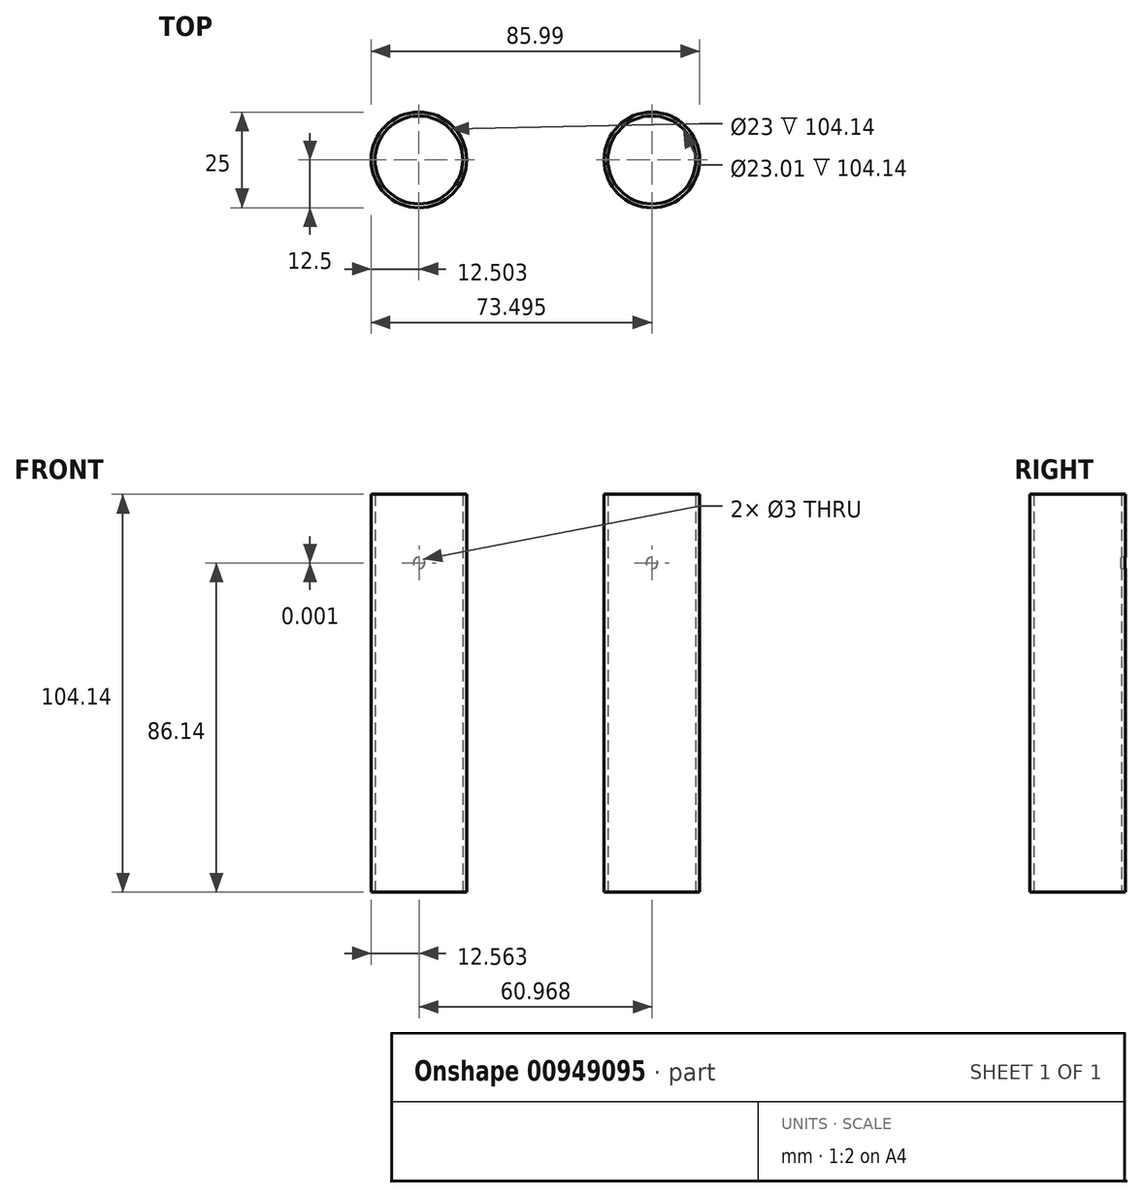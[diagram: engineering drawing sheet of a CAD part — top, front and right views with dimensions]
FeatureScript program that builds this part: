
annotation { "Feature Type Name" : "Feature", "Feature Type Description" : "" }
export const myFeature = defineFeature(function(context is Context, id is Id, definition is map)
    precondition{}
    {
        {
            var Q0;
            Q0=qCreatedBy(makeId("Top.planeOp"),FACE);
            var sketch = newSketch(context, id + "F0", { "sketchPlane" : qUnion([Q0])});
            skCircle(sketch, "E0", {"center": v(-36.28, 0) * mm, "radius": 11.5 * mm});
            skCircle(sketch, "E1", {"center": v(24.71, 0) * mm, "radius": 11.5 * mm});
            skPoint(sketch, "E2", {"position": v(13.2, 0) * mm});
            skPoint(sketch, "E3", {"position": v(-24.78, 0) * mm});
            skCircle(sketch, "E4", {"center": v(-36.28, 0) * mm, "radius": 12.5 * mm});
            skCircle(sketch, "E5", {"center": v(24.71, 0) * mm, "radius": 12.5 * mm});
            skPoint(sketch, "E6", {"position": v(-23.78, 0) * mm});
            skPoint(sketch, "E7", {"position": v(12.21, 0) * mm});
            skSolve(sketch);
        }
        {
            var Q0;
            Q0=makeQuery(id+"F0.imprint","IMPRINT",FACE,{"disambiguationData":[TD([[makeQuery(id+"F0.imprint","IMPRINT",EDGE,{"derivedFrom":sQuery(id+"F0.wireOp",EDGE,"E1")}),-1.0]])]});
            var Q1;
            Q1=makeQuery(id+"F0.imprint","IMPRINT",FACE,{"disambiguationData":[TD([[makeQuery(id+"F0.imprint","IMPRINT",EDGE,{"derivedFrom":sQuery(id+"F0.wireOp",EDGE,"E0")}),-1.0]])]});
            extrude(context, id + "F1", {"entities" : qUnion([Q0, Q1]), "depth" : 104.14 * mm, "offsetDistance" : 25.4 * mm, "symmetric" : true});
        }
        {
            var Q0;
            Q0=qCreatedBy(makeId("Front.planeOp"),FACE);
            var sketch = newSketch(context, id + "F2", { "sketchPlane" : qUnion([Q0])});
            skCircle(sketch, "E8", {"center": v(24.75, 34.07) * mm, "radius": 1.5 * mm});
            skCircle(sketch, "E9", {"center": v(-36.22, 34.07) * mm, "radius": 1.5 * mm});
            skLineSegment(sketch, "E10", {"start": v(37.21, 0) * mm, "end": v(12.3, 0) * mm});
            skPoint(sketch, "E11", {"position": v(24.75, 0) * mm});
            skLineSegment(sketch, "E12", {"start": v(-23.65, 0) * mm, "end": v(-48.79, 0) * mm});
            skPoint(sketch, "E13", {"position": v(-36.22, 0) * mm});
            skLineSegment(sketch, "E14", {"start": v(-36.22, 0) * mm, "end": v(-36.22, 34.07) * mm});
            skLineSegment(sketch, "E15", {"start": v(24.75, 0) * mm, "end": v(24.75, 34.07) * mm});
            skSolve(sketch);
        }
        {
            var Q0;
            {var subQ0=sQuery(id+"F2.wireOp",EDGE,"UVFeuSc1-rwqc-uxTH-lkc2-MKaSKzfGkuLp");var subQ1=sQuery(id+"F2.wireOp",EDGE,"E8");var subQ2=makeQuery(id+"F2.imprint","INTERSECT",VERTEX,{"disambiguationData":[OD(1.0)],"derivedFrom":[subQ1,subQ0]});Q0=makeQuery(id+"F2.imprint","IMPRINT",FACE,{"disambiguationData":[TD([[makeQuery(id+"F2.imprint","IMPRINT",EDGE,{"disambiguationData":[TD([[subQ2,1.0]])],"derivedFrom":subQ1}),1.0]])]});}
            var Q1;
            {var subQ0=sQuery(id+"F2.wireOp",EDGE,"UVFeuSc1-rwqc-uxTH-lkc2-MKaSKzfGkuLp");var subQ1=sQuery(id+"F2.wireOp",EDGE,"E8");var subQ2=makeQuery(id+"F2.imprint","INTERSECT",VERTEX,{"disambiguationData":[OD(0.0)],"derivedFrom":[subQ1,subQ0]});Q1=makeQuery(id+"F2.imprint","IMPRINT",FACE,{"disambiguationData":[TD([[makeQuery(id+"F2.imprint","IMPRINT",EDGE,{"disambiguationData":[TD([[subQ2,1.0]])],"derivedFrom":subQ1}),1.0]])]});}
            var Q2;
            {var subQ0=sQuery(id+"F2.wireOp",EDGE,"UVFeuSc1-rwqc-uxTH-lkc2-MKaSKzfGkuLp");var subQ1=sQuery(id+"F2.wireOp",EDGE,"E8");var subQ2=makeQuery(id+"F2.imprint","INTERSECT",VERTEX,{"disambiguationData":[OD(0.0)],"derivedFrom":[subQ1,subQ0]});Q2=makeQuery(id+"F2.imprint","IMPRINT",FACE,{"disambiguationData":[TD([[makeQuery(id+"F2.imprint","IMPRINT",EDGE,{"disambiguationData":[TD([[subQ2,-1.0]])],"derivedFrom":subQ1}),1.0]])]});}
            var Q3;
            Q3=makeQuery(id+"F2.imprint","IMPRINT",FACE,{"disambiguationData":[TD([[makeQuery(id+"F2.imprint","IMPRINT",EDGE,{"derivedFrom":sQuery(id+"F2.wireOp",EDGE,"E9")}),1.0]])]});
            extrude(context, id + "F3", {"entities" : qUnion([Q0, Q1, Q2, Q3]), "operationType" : NewBodyOperationType.REMOVE, "oppositeDirection" : true, "depth" : 34.04 * mm, "offsetDistance" : 25.4 * mm});
        }
    });
